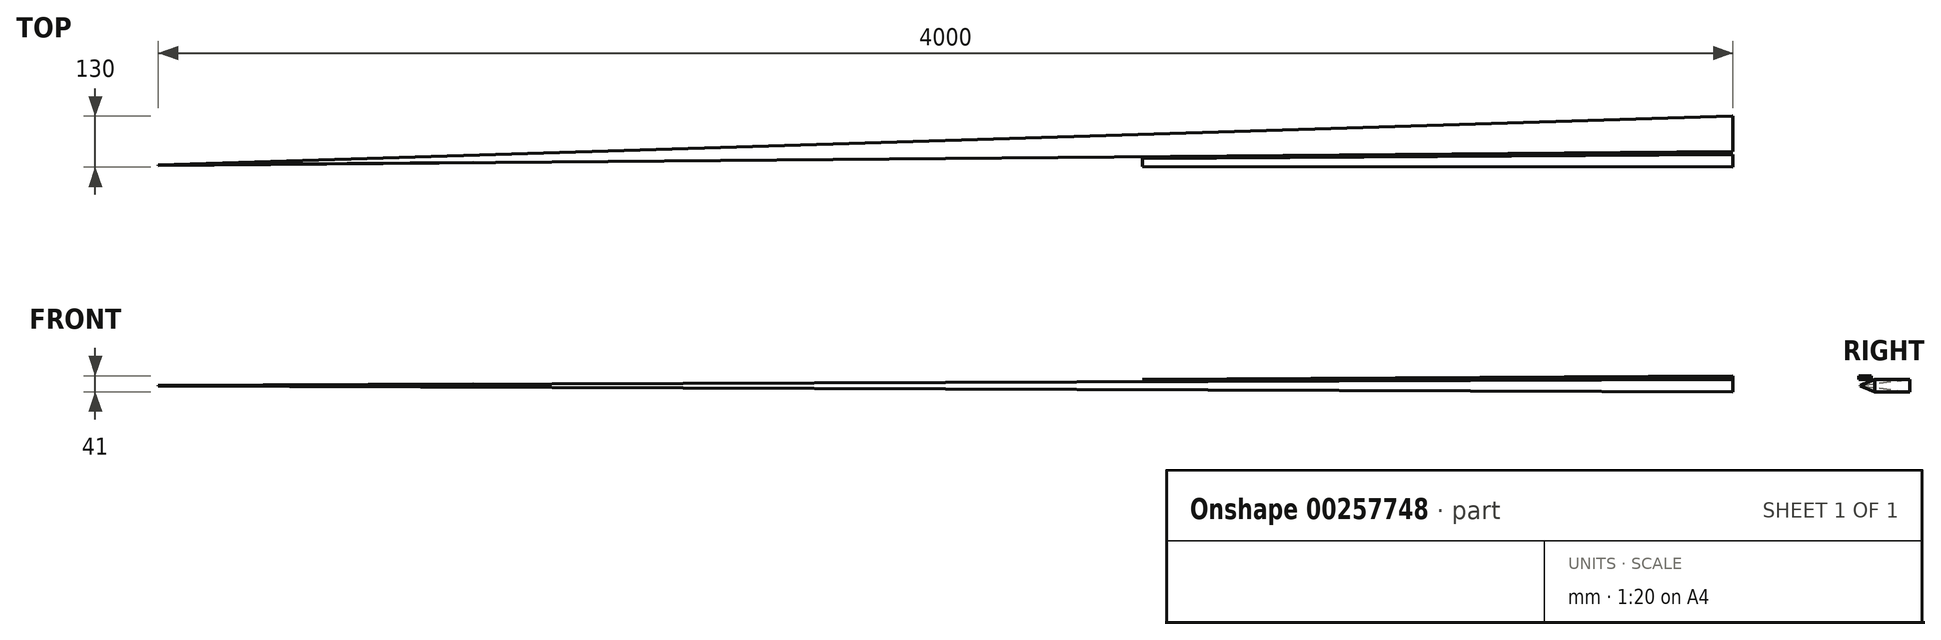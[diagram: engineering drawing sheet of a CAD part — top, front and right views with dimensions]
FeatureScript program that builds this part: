
annotation { "Feature Type Name" : "Feature", "Feature Type Description" : "" }
export const myFeature = defineFeature(function(context is Context, id is Id, definition is map)
    precondition{}
    {
        {
            var Q0;
            Q0=qCreatedBy(makeId("Right.planeOp"),FACE);
            var sketch = newSketch(context, id + "F0", { "sketchPlane" : qUnion([Q0])});
            skLineSegment(sketch, "E0.bottom", {"start": v(-5, 25) * mm, "end": v(27, 25) * mm});
            skLineSegment(sketch, "E0.top", {"start": v(-5, -65) * mm, "end": v(27, -65) * mm});
            skLineSegment(sketch, "E0.left", {"start": v(-5, 25) * mm, "end": v(-5, -65) * mm});
            skLineSegment(sketch, "E0.right", {"start": v(27, 25) * mm, "end": v(27, -65) * mm});
            skSolve(sketch);
        }
        {
            var Q0;
            Q0=makeQuery(id+"F0.imprint","IMPRINT",FACE,{"disambiguationData":[TD([[makeQuery(id+"F0.imprint","IMPRINT",EDGE,{"derivedFrom":sQuery(id+"F0.wireOp",EDGE,"E0.bottom")}),-1.0]])]});
            extrude(context, id + "F1", {"entities" : qUnion([Q0]), "depth" : 4000 * mm});
        }
        {
            var Q0;
            Q0=makeQuery(id+"F1.opExtrude","SWEPT_FACE",FACE,{"disambiguationData":[OSD([sQuery(id+"F0.wireOp",EDGE,"E0.left")])]});
            var sketch = newSketch(context, id + "F2", { "sketchPlane" : qUnion([Q0])});
            skLineSegment(sketch, "E1", {"start": v(0, 1) * mm, "end": v(4000, 25) * mm});
            skLineSegment(sketch, "E2", {"start": v(4000, 25) * mm, "end": v(0, 25) * mm});
            skLineSegment(sketch, "E3", {"start": v(0, 25) * mm, "end": v(0, 1) * mm});
            skLineSegment(sketch, "E4", {"start": v(0, -1) * mm, "end": v(0, -65) * mm});
            skLineSegment(sketch, "E5", {"start": v(0, -65) * mm, "end": v(4000, -65) * mm});
            skLineSegment(sketch, "E6", {"start": v(4000, -65) * mm, "end": v(0, -1) * mm});
            skSolve(sketch);
        }
        {
            var Q0;
            Q0=makeQuery(id+"F2.imprint","IMPRINT",FACE,{"disambiguationData":[TD([[makeQuery(id+"F2.imprint","IMPRINT",EDGE,{"derivedFrom":sQuery(id+"F2.wireOp",EDGE,"E1")}),1.0]])]});
            var Q1;
            Q1=makeQuery(id+"F2.imprint","IMPRINT",FACE,{"disambiguationData":[TD([[makeQuery(id+"F2.imprint","IMPRINT",EDGE,{"derivedFrom":sQuery(id+"F2.wireOp",EDGE,"E4")}),1.0]])]});
            extrude(context, id + "F3", {"entities" : qUnion([Q0, Q1]), "operationType" : NewBodyOperationType.REMOVE, "endBound" : BoundingType.THROUGH_ALL, "oppositeDirection" : true, "depth" : 25 * mm});
        }
        {
            var Q0;
            Q0=makeQuery(id+"F3.boolean.opBoolean","COPY",FACE,{"derivedFrom":makeQuery(id+"F3.opExtrude","SWEPT_FACE",FACE,{"disambiguationData":[OSD([sQuery(id+"F2.wireOp",EDGE,"E1")])]})});
            var sketch = newSketch(context, id + "F4", { "sketchPlane" : qUnion([Q0])});
            skLineSegment(sketch, "E7", {"start": v(0, 1) * mm, "end": v(0, 27) * mm});
            skLineSegment(sketch, "E8", {"start": v(0, 27) * mm, "end": v(4000.08, 27) * mm});
            skLineSegment(sketch, "E9", {"start": v(4000.08, 27) * mm, "end": v(0, 1) * mm});
            skLineSegment(sketch, "E10", {"start": v(0, -1) * mm, "end": v(0, -5) * mm});
            skLineSegment(sketch, "E11", {"start": v(0, -5) * mm, "end": v(4000.08, -5) * mm});
            skLineSegment(sketch, "E12", {"start": v(4000.08, -5) * mm, "end": v(0, -1) * mm});
            skSolve(sketch);
        }
        {
            var Q0;
            Q0=makeQuery(id+"F4.imprint","IMPRINT",FACE,{"disambiguationData":[TD([[makeQuery(id+"F4.imprint","IMPRINT",EDGE,{"derivedFrom":sQuery(id+"F4.wireOp",EDGE,"E7")}),1.0]])]});
            var Q1;
            Q1=makeQuery(id+"F4.imprint","IMPRINT",FACE,{"disambiguationData":[TD([[makeQuery(id+"F4.imprint","IMPRINT",EDGE,{"derivedFrom":sQuery(id+"F4.wireOp",EDGE,"E10")}),1.0]])]});
            extrude(context, id + "F5", {"entities" : qUnion([Q0, Q1]), "operationType" : NewBodyOperationType.REMOVE, "endBound" : BoundingType.THROUGH_ALL, "oppositeDirection" : true, "depth" : 25 * mm});
        }
        {
            var Q0;
            Q0=makeQuery(id+"F5.boolean.opBoolean","COPY",FACE,{"derivedFrom":makeQuery(id+"F5.opExtrude","SWEPT_FACE",FACE,{"disambiguationData":[OSD([sQuery(id+"F4.wireOp",EDGE,"E10")])]})});
            var Q1;
            Q1=makeQuery(id+"F5.boolean.opBoolean","COPY",FACE,{"derivedFrom":makeQuery(id+"F5.opExtrude","SWEPT_FACE",FACE,{"disambiguationData":[OSD([sQuery(id+"F4.wireOp",EDGE,"E7")])]})});
            extrude(context, id + "F6", {"entities" : qUnion([Q0, Q1]), "operationType" : NewBodyOperationType.REMOVE, "endBound" : BoundingType.THROUGH_ALL, "oppositeDirection" : true, "depth" : 25 * mm});
        }
        {
            var Q0;
            Q0=qCreatedBy(makeId("Right.planeOp"),FACE);
            var sketch = newSketch(context, id + "F7", { "sketchPlane" : qUnion([Q0])});
            skLineSegment(sketch, "E13.bottom", {"start": v(125, 16) * mm, "end": v(35, 16) * mm});
            skLineSegment(sketch, "E13.top", {"start": v(125, -16) * mm, "end": v(35, -16) * mm});
            skLineSegment(sketch, "E13.left", {"start": v(125, 16) * mm, "end": v(125, -16) * mm});
            skLineSegment(sketch, "E13.right", {"start": v(35, 16) * mm, "end": v(35, -16) * mm});
            skLineSegment(sketch, "E14.bottom", {"start": v(35, 16) * mm, "end": v(-10, 16) * mm});
            skLineSegment(sketch, "E14.top", {"start": v(35, -16) * mm, "end": v(-10, -16) * mm});
            skLineSegment(sketch, "E14.left", {"start": v(35, 16) * mm, "end": v(35, -16) * mm, "construction": true});
            skLineSegment(sketch, "E14.right", {"start": v(-10, 16) * mm, "end": v(-10, -16) * mm});
            skSolve(sketch);
        }
        {
            var Q0;
            Q0=makeQuery(id+"F7.imprint","IMPRINT",FACE,{"disambiguationData":[TD([[makeQuery(id+"F7.imprint","IMPRINT",EDGE,{"derivedFrom":sQuery(id+"F7.wireOp",EDGE,"E13.bottom")}),1.0]])]});
            var Q1;
            Q1=makeQuery(id+"F7.imprint","IMPRINT",FACE,{"disambiguationData":[TD([[makeQuery(id+"F7.imprint","IMPRINT",EDGE,{"derivedFrom":sQuery(id+"F7.wireOp",EDGE,"E13.right")}),-1.0]])]});
            extrude(context, id + "F8", {"entities" : qUnion([Q0, Q1]), "depth" : 4000 * mm});
        }
        {
            var Q0;
            Q0=makeQuery(id+"F8.opExtrude","SWEPT_FACE",FACE,{"disambiguationData":[OSD([sQuery(id+"F7.wireOp",EDGE,"E13.bottom"),sQuery(id+"F7.wireOp",EDGE,"E14.bottom")])]});
            var sketch = newSketch(context, id + "F9", { "sketchPlane" : qUnion([Q0])});
            skLineSegment(sketch, "E15", {"start": v(0, -1) * mm, "end": v(0, -10) * mm});
            skLineSegment(sketch, "E16", {"start": v(0, -10) * mm, "end": v(4000, -10) * mm});
            skLineSegment(sketch, "E17", {"start": v(4000, -10) * mm, "end": v(4000, 35) * mm});
            skLineSegment(sketch, "E18", {"start": v(4000, 35) * mm, "end": v(0, -1) * mm});
            skLineSegment(sketch, "E19", {"start": v(0, 1) * mm, "end": v(0, 125) * mm});
            skLineSegment(sketch, "E20", {"start": v(0, 125) * mm, "end": v(4000, 125) * mm});
            skLineSegment(sketch, "E21", {"start": v(4000, 125) * mm, "end": v(0, 1) * mm});
            skSolve(sketch);
        }
        {
            var Q0;
            Q0=makeQuery(id+"F9.imprint","IMPRINT",FACE,{"disambiguationData":[TD([[makeQuery(id+"F9.imprint","IMPRINT",EDGE,{"derivedFrom":sQuery(id+"F9.wireOp",EDGE,"E15")}),1.0]])]});
            var Q1;
            Q1=makeQuery(id+"F9.imprint","IMPRINT",FACE,{"disambiguationData":[TD([[makeQuery(id+"F9.imprint","IMPRINT",EDGE,{"derivedFrom":sQuery(id+"F9.wireOp",EDGE,"E19")}),1.0]])]});
            extrude(context, id + "F10", {"entities" : qUnion([Q0, Q1]), "operationType" : NewBodyOperationType.REMOVE, "endBound" : BoundingType.THROUGH_ALL, "oppositeDirection" : true, "depth" : 25 * mm});
        }
        {
            var Q0;
            Q0=makeQuery(id+"F10.boolean.opBoolean","COPY",FACE,{"derivedFrom":makeQuery(id+"F10.opExtrude","SWEPT_FACE",FACE,{"disambiguationData":[OSD([sQuery(id+"F9.wireOp",EDGE,"E18")])]})});
            var sketch = newSketch(context, id + "F11", { "sketchPlane" : qUnion([Q0])});
            skLineSegment(sketch, "E22", {"start": v(0, 1) * mm, "end": v(0, 16) * mm});
            skLineSegment(sketch, "E23", {"start": v(0, 16) * mm, "end": v(4000.15, 16) * mm});
            skLineSegment(sketch, "E24", {"start": v(4000.15, 16) * mm, "end": v(0, 1) * mm});
            skLineSegment(sketch, "E25", {"start": v(0, -1) * mm, "end": v(0, -16) * mm});
            skLineSegment(sketch, "E26", {"start": v(0, -16) * mm, "end": v(4000.15, -16) * mm});
            skLineSegment(sketch, "E27", {"start": v(4000.15, -16) * mm, "end": v(0, -1) * mm});
            skSolve(sketch);
        }
        {
            var Q0;
            Q0=makeQuery(id+"F11.imprint","IMPRINT",FACE,{"disambiguationData":[TD([[makeQuery(id+"F11.imprint","IMPRINT",EDGE,{"derivedFrom":sQuery(id+"F11.wireOp",EDGE,"E22")}),-1.0]])]});
            var Q1;
            Q1=makeQuery(id+"F11.imprint","IMPRINT",FACE,{"disambiguationData":[TD([[makeQuery(id+"F11.imprint","IMPRINT",EDGE,{"derivedFrom":sQuery(id+"F11.wireOp",EDGE,"E25")}),-1.0]])]});
            extrude(context, id + "F12", {"entities" : qUnion([Q0, Q1]), "operationType" : NewBodyOperationType.REMOVE, "endBound" : BoundingType.THROUGH_ALL, "oppositeDirection" : true, "depth" : 25 * mm});
        }
    });
